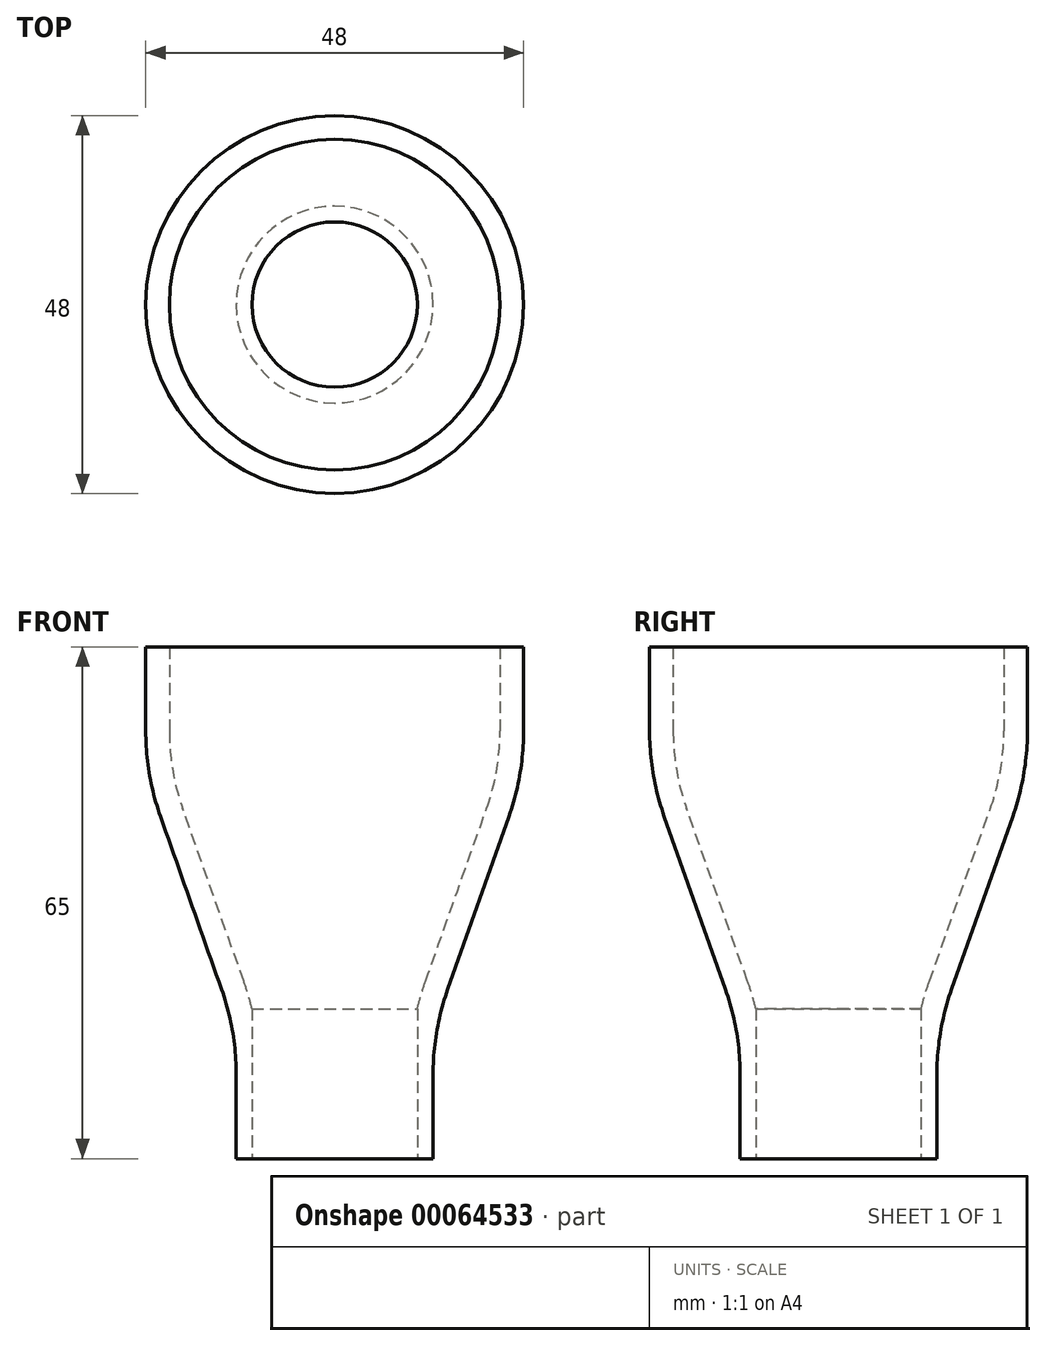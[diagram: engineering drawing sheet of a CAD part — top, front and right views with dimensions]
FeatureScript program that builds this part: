
annotation { "Feature Type Name" : "Feature", "Feature Type Description" : "" }
export const myFeature = defineFeature(function(context is Context, id is Id, definition is map)
    precondition{}
    {
        {
            assignVariable(context, id + "F0", {"name" : "B2", "anyValue" : 3});
        }
        {
            var Q0;
            Q0=qCreatedBy(makeId("Front.planeOp"),FACE);
            var sketch = newSketch(context, id + "F1", { "sketchPlane" : qUnion([Q0])});
            skLineSegment(sketch, "E0", {"start": v(0, 0) * mm, "end": v(0, 65) * mm});
            skLineSegment(sketch, "E1", {"start": v(0, 65) * mm, "end": v(24, 65) * mm});
            skLineSegment(sketch, "E2", {"start": v(0, 0) * mm, "end": v(12.5, 0) * mm});
            skLineSegment(sketch, "E3", {"start": v(24, 65) * mm, "end": v(24, 54.33) * mm});
            skLineSegment(sketch, "E4", {"start": v(12.5, 0) * mm, "end": v(12.5, 10.67) * mm});
            skLineSegment(sketch, "E5", {"start": v(22.14, 43.49) * mm, "end": v(14.36, 21.51) * mm});
            skPoint(sketch, "E6.visualSharp", {"position": v(24, 48.75) * mm});
            skArc(sketch, "E6.filletArc", {"start": v(22.14, 43.49) * mm, "mid": v(23.53, 48.83) * mm, "end": v(24, 54.33) * mm});
            skPoint(sketch, "E7.visualSharp", {"position": v(12.5, 16.25) * mm});
            skArc(sketch, "E7.filletArc", {"start": v(14.36, 21.51) * mm, "mid": v(12.97, 16.17) * mm, "end": v(12.5, 10.67) * mm});
            skSolve(sketch);
        }
        {
            var Q0;
            Q0=makeQuery(id+"F1.imprint","IMPRINT",FACE,{"disambiguationData":[TD([[makeQuery(id+"F1.imprint","IMPRINT",EDGE,{"derivedFrom":sQuery(id+"F1.wireOp",EDGE,"E0")}),-1.0]])]});
            var Q1;
            Q1=sQuery(id+"F1.wireOp",EDGE,"E0");
            revolve(context, id + "F2", {"entities" : qUnion([Q0]), "axis" : qUnion([Q1]), "revolveType" : RevolveType.FULL});
        }
        {
            var Q0;
            Q0=makeQuery(id+"F2.opRevolve","SWEPT_FACE",FACE,{"disambiguationData":[OSD([sQuery(id+"F1.wireOp",EDGE,"E1")])]});
            var sketch = newSketch(context, id + "F3", { "sketchPlane" : qUnion([Q0])});
            skCircle(sketch, "E8", {"center": v(0, 0) * mm, "radius": 21 * mm});
            skSolve(sketch);
        }
        {
            var Q0;
            Q0=makeQuery(id+"F2.opRevolve","SWEPT_FACE",FACE,{"disambiguationData":[OSD([sQuery(id+"F1.wireOp",EDGE,"E2")])]});
            var sketch = newSketch(context, id + "F4", { "sketchPlane" : qUnion([Q0])});
            skCircle(sketch, "E9", {"center": v(0, 0) * mm, "radius": 10.5 * mm});
            skSolve(sketch);
        }
        {
            var Q0;
            Q0=makeQuery(id+"F2.opRevolve","SWEPT_FACE",FACE,{"disambiguationData":[OSD([sQuery(id+"F1.wireOp",EDGE,"E1")])]});
            var Q1;
            Q1=makeQuery(id+"F2.opRevolve","SWEPT_BODY",BODY,{"disambiguationData":[OSD([sQuery(id+"F1.wireOp",EDGE,"E0"),sQuery(id+"F1.wireOp",EDGE,"E1"),sQuery(id+"F1.wireOp",EDGE,"E2"),sQuery(id+"F1.wireOp",EDGE,"E3"),sQuery(id+"F1.wireOp",EDGE,"E4"),sQuery(id+"F1.wireOp",EDGE,"E5"),sQuery(id+"F1.wireOp",EDGE,"E6.filletArc"),sQuery(id+"F1.wireOp",EDGE,"E7.filletArc")])]});
            shell(context, id + "F5", {"entities" : qUnion([Q0]), "parts" : qUnion([Q1]), "thickness" : (getVariable(context, 'B2')) * mm});
        }
        {
            var Q0;
            Q0=qSketchRegion(id+"F4",true);
            extrude(context, id + "F6", {"entities" : qUnion([Q0]), "operationType" : NewBodyOperationType.REMOVE, "endBound" : BoundingType.THROUGH_ALL, "oppositeDirection" : true, "depth" : 25 * mm});
        }
    });
